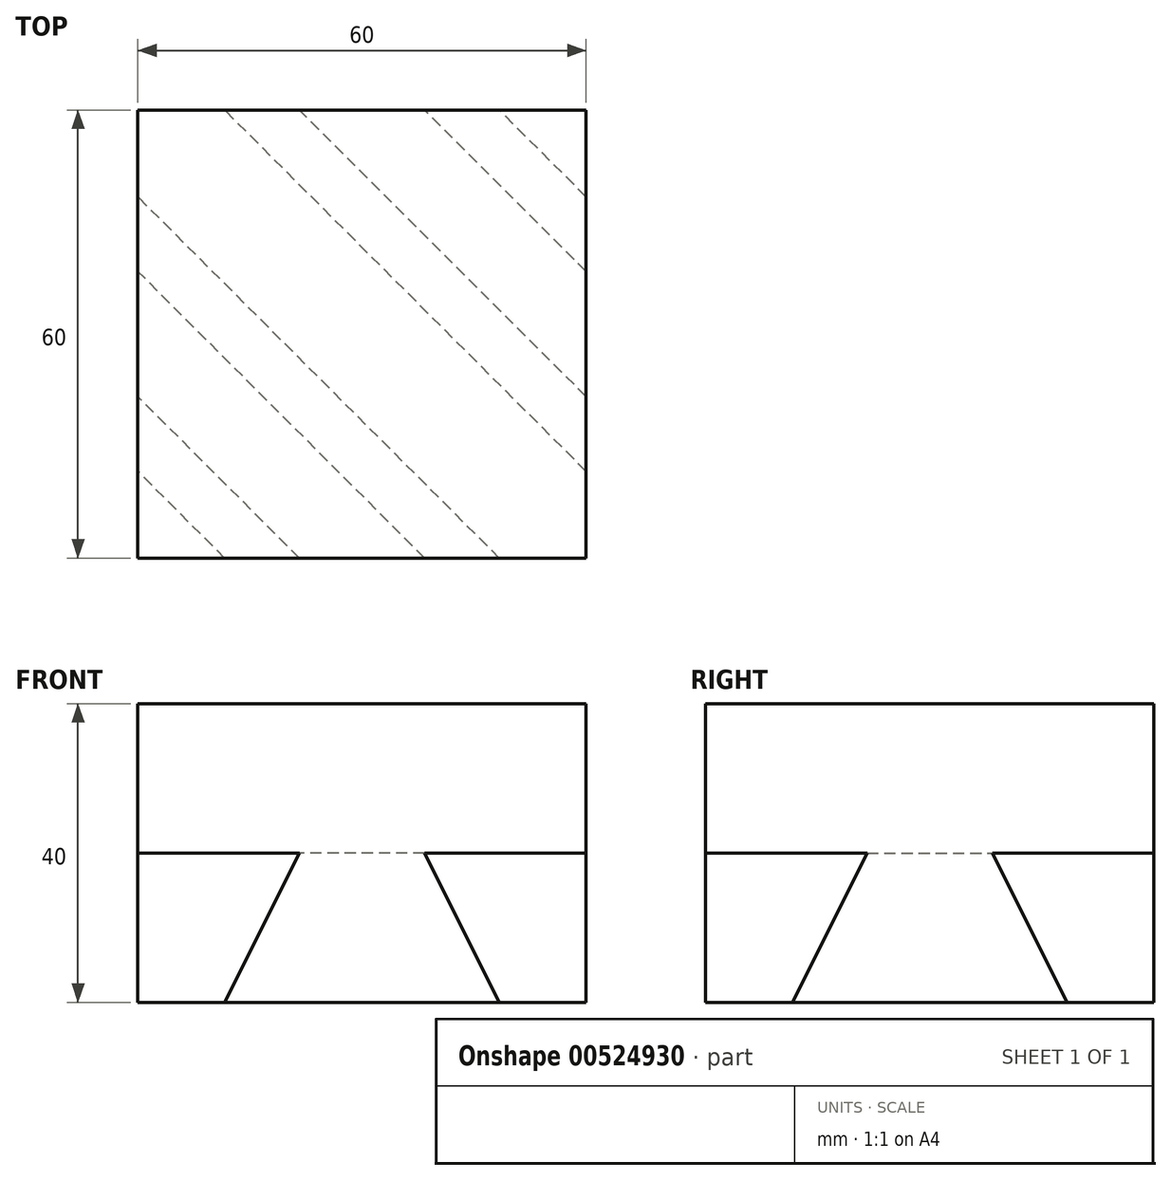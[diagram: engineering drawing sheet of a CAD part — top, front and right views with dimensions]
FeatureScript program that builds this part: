
annotation { "Feature Type Name" : "Feature", "Feature Type Description" : "" }
export const myFeature = defineFeature(function(context is Context, id is Id, definition is map)
    precondition{}
    {
        {
            var Q0;
            Q0=qCreatedBy(makeId("Front.planeOp"),FACE);
            var sketch = newSketch(context, id + "F0", { "sketchPlane" : qUnion([Q0])});
            skLineSegment(sketch, "E0", {"start": v(0, 70.49) * mm, "end": v(0, -41.75) * mm, "construction": true});
            skSolve(sketch);
        }
        {
            var Q0;
            Q0=qCreatedBy(makeId("Top.planeOp"),FACE);
            var sketch = newSketch(context, id + "F1", { "sketchPlane" : qUnion([Q0])});
            skLineSegment(sketch, "E1.bottom", {"start": v(30, 30) * mm, "end": v(-30, 30) * mm});
            skLineSegment(sketch, "E1.top", {"start": v(30, -30) * mm, "end": v(-30, -30) * mm});
            skLineSegment(sketch, "E1.left", {"start": v(30, 30) * mm, "end": v(30, -30) * mm});
            skLineSegment(sketch, "E1.right", {"start": v(-30, 30) * mm, "end": v(-30, -30) * mm});
            skPoint(sketch, "E1.middle", {"position": v(0, 0) * mm});
            skSolve(sketch);
        }
        {
            var Q0;
            Q0=qSketchRegion(id+"F1",true);
            extrude(context, id + "F2", {"entities" : qUnion([Q0]), "depth" : 60 * mm, "offsetDistance" : 25 * mm});
        }
        {
            var Q0;
            Q0=makeQuery(id+"F2.opExtrude","SWEPT_FACE",FACE,{"disambiguationData":[OSD([sQuery(id+"F1.wireOp",EDGE,"E1.top")])]});
            var sketch = newSketch(context, id + "F3", { "sketchPlane" : qUnion([Q0])});
            skLineSegment(sketch, "E2", {"start": v(-10, 40) * mm, "end": v(-20, 20) * mm, "construction": true});
            skLineSegment(sketch, "E3", {"start": v(20, 20) * mm, "end": v(10, 40) * mm, "construction": true});
            skLineSegment(sketch, "E4", {"start": v(-20, 20) * mm, "end": v(0, 20) * mm, "construction": true});
            skLineSegment(sketch, "E5", {"start": v(0, 20) * mm, "end": v(20, 20) * mm, "construction": true});
            skLineSegment(sketch, "E6", {"start": v(-10, 40) * mm, "end": v(10, 40) * mm, "construction": true});
            skLineSegment(sketch, "E7", {"start": v(-10, 40) * mm, "end": v(-30, 40) * mm, "construction": true});
            skLineSegment(sketch, "E8", {"start": v(10, 40) * mm, "end": v(30, 40) * mm, "construction": true});
            skLineSegment(sketch, "E9.0", {"start": v(-8.38, 41) * mm, "end": v(-30, 41) * mm});
            skLineSegment(sketch, "E9.1", {"start": v(-8.38, 41) * mm, "end": v(-18.38, 21) * mm});
            skLineSegment(sketch, "E9.2", {"start": v(8.38, 41) * mm, "end": v(30, 41) * mm});
            skLineSegment(sketch, "E9.3", {"start": v(18.38, 21) * mm, "end": v(8.38, 41) * mm});
            skLineSegment(sketch, "E9.4", {"start": v(0, 21) * mm, "end": v(18.38, 21) * mm});
            skLineSegment(sketch, "E9.5", {"start": v(-18.38, 21) * mm, "end": v(0, 21) * mm});
            skLineSegment(sketch, "E10", {"start": v(-8.38, 41) * mm, "end": v(8.38, 41) * mm});
            skSolve(sketch);
        }
        {
            var Q0;
            Q0=makeQuery(id+"F2.opExtrude","SWEPT_FACE",FACE,{"disambiguationData":[OSD([sQuery(id+"F1.wireOp",EDGE,"E1.left")])]});
            var sketch = newSketch(context, id + "F4", { "sketchPlane" : qUnion([Q0])});
            skLineSegment(sketch, "E11", {"start": v(-10, 40) * mm, "end": v(-20, 20) * mm, "construction": true});
            skLineSegment(sketch, "E12", {"start": v(20, 20) * mm, "end": v(10, 40) * mm, "construction": true});
            skLineSegment(sketch, "E13", {"start": v(-20, 20) * mm, "end": v(0, 20) * mm, "construction": true});
            skLineSegment(sketch, "E14", {"start": v(0, 20) * mm, "end": v(20, 20) * mm, "construction": true});
            skLineSegment(sketch, "E15", {"start": v(-10, 40) * mm, "end": v(10, 40) * mm, "construction": true});
            skLineSegment(sketch, "E16", {"start": v(-10, 40) * mm, "end": v(-30, 40) * mm, "construction": true});
            skLineSegment(sketch, "E17", {"start": v(10, 40) * mm, "end": v(30, 40) * mm, "construction": true});
            skLineSegment(sketch, "E18.0", {"start": v(-8.38, 41) * mm, "end": v(-30, 41) * mm});
            skLineSegment(sketch, "E18.1", {"start": v(-8.38, 41) * mm, "end": v(-18.38, 21) * mm});
            skLineSegment(sketch, "E18.2", {"start": v(8.38, 41) * mm, "end": v(30, 41) * mm});
            skLineSegment(sketch, "E18.3", {"start": v(18.38, 21) * mm, "end": v(8.38, 41) * mm});
            skLineSegment(sketch, "E18.4", {"start": v(0, 21) * mm, "end": v(18.38, 21) * mm});
            skLineSegment(sketch, "E18.5", {"start": v(-18.38, 21) * mm, "end": v(0, 21) * mm});
            skLineSegment(sketch, "E19", {"start": v(-8.38, 41) * mm, "end": v(8.38, 41) * mm});
            skSolve(sketch);
        }
        {
            var Q0;
            Q0=makeQuery(id+"F2.opExtrude","SWEPT_FACE",FACE,{"disambiguationData":[OSD([sQuery(id+"F1.wireOp",EDGE,"E1.bottom")])]});
            var sketch = newSketch(context, id + "F5", { "sketchPlane" : qUnion([Q0])});
            skLineSegment(sketch, "E20", {"start": v(-10, 40) * mm, "end": v(-20, 20) * mm, "construction": true});
            skLineSegment(sketch, "E21", {"start": v(20, 20) * mm, "end": v(10, 40) * mm, "construction": true});
            skLineSegment(sketch, "E22", {"start": v(-20, 20) * mm, "end": v(0, 20) * mm, "construction": true});
            skLineSegment(sketch, "E23", {"start": v(0, 20) * mm, "end": v(20, 20) * mm, "construction": true});
            skLineSegment(sketch, "E24", {"start": v(-10, 40) * mm, "end": v(10, 40) * mm, "construction": true});
            skLineSegment(sketch, "E25", {"start": v(-10, 40) * mm, "end": v(-30, 40) * mm, "construction": true});
            skLineSegment(sketch, "E26", {"start": v(10, 40) * mm, "end": v(30, 40) * mm, "construction": true});
            skLineSegment(sketch, "E27.0", {"start": v(-8.38, 41) * mm, "end": v(-30, 41) * mm});
            skLineSegment(sketch, "E27.1", {"start": v(-8.38, 41) * mm, "end": v(-18.38, 21) * mm});
            skLineSegment(sketch, "E27.2", {"start": v(8.38, 41) * mm, "end": v(30, 41) * mm});
            skLineSegment(sketch, "E27.3", {"start": v(18.38, 21) * mm, "end": v(8.38, 41) * mm});
            skLineSegment(sketch, "E27.4", {"start": v(0, 21) * mm, "end": v(18.38, 21) * mm});
            skLineSegment(sketch, "E27.5", {"start": v(-18.38, 21) * mm, "end": v(0, 21) * mm});
            skLineSegment(sketch, "E28", {"start": v(8.38, 41) * mm, "end": v(-8.38, 41) * mm});
            skSolve(sketch);
        }
        {
            var Q0;
            Q0=makeQuery(id+"F2.opExtrude","SWEPT_FACE",FACE,{"disambiguationData":[OSD([sQuery(id+"F1.wireOp",EDGE,"E1.right")])]});
            var sketch = newSketch(context, id + "F6", { "sketchPlane" : qUnion([Q0])});
            skLineSegment(sketch, "E29", {"start": v(-10, 40) * mm, "end": v(-20, 20) * mm, "construction": true});
            skLineSegment(sketch, "E30", {"start": v(20, 20) * mm, "end": v(10, 40) * mm, "construction": true});
            skLineSegment(sketch, "E31", {"start": v(-20, 20) * mm, "end": v(0, 20) * mm, "construction": true});
            skLineSegment(sketch, "E32", {"start": v(0, 20) * mm, "end": v(20, 20) * mm, "construction": true});
            skLineSegment(sketch, "E33", {"start": v(-10, 40) * mm, "end": v(10, 40) * mm, "construction": true});
            skLineSegment(sketch, "E34", {"start": v(-10, 40) * mm, "end": v(-30, 40) * mm, "construction": true});
            skLineSegment(sketch, "E35", {"start": v(10, 40) * mm, "end": v(30, 40) * mm, "construction": true});
            skLineSegment(sketch, "E36.0", {"start": v(-8.38, 41) * mm, "end": v(-30, 41) * mm});
            skLineSegment(sketch, "E36.1", {"start": v(-8.38, 41) * mm, "end": v(-18.38, 21) * mm});
            skLineSegment(sketch, "E36.2", {"start": v(8.38, 41) * mm, "end": v(30, 41) * mm});
            skLineSegment(sketch, "E36.3", {"start": v(18.38, 21) * mm, "end": v(8.38, 41) * mm});
            skLineSegment(sketch, "E36.4", {"start": v(0, 21) * mm, "end": v(18.38, 21) * mm});
            skLineSegment(sketch, "E36.5", {"start": v(-18.38, 21) * mm, "end": v(0, 21) * mm});
            skLineSegment(sketch, "E37", {"start": v(-8.38, 41) * mm, "end": v(8.38, 41) * mm});
            skSolve(sketch);
        }
        {
            var Q1;
            Q1=makeQuery(id+"F3.imprint","IMPRINT",FACE,{"disambiguationData":[TD([[makeQuery(id+"F3.imprint","IMPRINT",EDGE,{"derivedFrom":sQuery(id+"F3.wireOp",EDGE,"E9.1")}),1.0]])]});
            var Q2;
            Q2=makeQuery(id+"F6.imprint","IMPRINT",FACE,{"disambiguationData":[TD([[makeQuery(id+"F6.imprint","IMPRINT",EDGE,{"derivedFrom":sQuery(id+"F6.wireOp",EDGE,"E36.1")}),1.0]])]});
            loft(context, id + "F7", {"operationType" : NewBodyOperationType.REMOVE, "sheetProfilesArray" : [{ "sheetProfileEntities" : qUnion([Q1]) }, { "sheetProfileEntities" : qUnion([Q2]) }]});
        }
        {
            var Q1;
            Q1=makeQuery(id+"F4.imprint","IMPRINT",FACE,{"disambiguationData":[TD([[makeQuery(id+"F4.imprint","IMPRINT",EDGE,{"derivedFrom":sQuery(id+"F4.wireOp",EDGE,"E18.1")}),1.0]])]});
            var Q2;
            Q2=makeQuery(id+"F5.imprint","IMPRINT",FACE,{"disambiguationData":[TD([[makeQuery(id+"F5.imprint","IMPRINT",EDGE,{"derivedFrom":sQuery(id+"F5.wireOp",EDGE,"E27.1")}),1.0]])]});
            loft(context, id + "F8", {"operationType" : NewBodyOperationType.REMOVE, "sheetProfilesArray" : [{ "sheetProfileEntities" : qUnion([Q1]) }, { "sheetProfileEntities" : qUnion([Q2]) }]});
        }
        {
            var Q0;
            Q0=makeQuery(id+"F2.opExtrude","SWEPT_FACE",FACE,{"disambiguationData":[OSD([sQuery(id+"F1.wireOp",EDGE,"E1.top")])]});
            var sketch = newSketch(context, id + "F9", { "sketchPlane" : qUnion([Q0])});
            skLineSegment(sketch, "E38.bottom", {"start": v(-30, 60) * mm, "end": v(30, 60) * mm});
            skLineSegment(sketch, "E38.top", {"start": v(-30, 41) * mm, "end": v(30, 41) * mm});
            skLineSegment(sketch, "E38.left", {"start": v(-30, 60) * mm, "end": v(-30, 41) * mm});
            skLineSegment(sketch, "E38.right", {"start": v(30, 60) * mm, "end": v(30, 41) * mm});
            skSolve(sketch);
        }
        {
            var Q0;
            Q0 = qSketchRegion(id + "F9", true);
            extrude(context, id + "F10", {"entities" : qUnion([Q0]), "operationType" : NewBodyOperationType.REMOVE, "oppositeDirection" : true, "depth" : 60 * mm, "offsetDistance" : 25 * mm});
        }
        {
            var Q0;
            Q0=makeQuery(id+"F10.boolean.opBoolean","COPY",FACE,{"disambiguationData":[TD([makeQuery(id+"F7.boolean.opBoolean","COPY",FACE,{"derivedFrom":makeQuery(id+"F7.opLoft","SWEPT_FACE",FACE,{"disambiguationData":[OSD([sQuery(id+"F3.wireOp",EDGE,"E9.2"),sQuery(id+"F3.wireOp",EDGE,"E9.3"),sQuery(id+"F3.wireOp",EDGE,"E9.4"),sQuery(id+"F3.wireOp",EDGE,"E10"),sQuery(id+"F6.wireOp",EDGE,"E36.0"),sQuery(id+"F6.wireOp",EDGE,"E36.1"),sQuery(id+"F6.wireOp",EDGE,"E36.5"),sQuery(id+"F6.wireOp",EDGE,"E37")])]})})])],"derivedFrom":makeQuery(id+"F10.opExtrude","SWEPT_FACE",FACE,{"disambiguationData":[OSD([sQuery(id+"F9.wireOp",EDGE,"E38.top")])]})});
            var sketch = newSketch(context, id + "F11", { "sketchPlane" : qUnion([Q0])});
            skLineSegment(sketch, "E39.bottom", {"start": v(-30, 30) * mm, "end": v(30, 30) * mm});
            skLineSegment(sketch, "E39.top", {"start": v(-30, -30) * mm, "end": v(30, -30) * mm});
            skLineSegment(sketch, "E39.left", {"start": v(-30, 30) * mm, "end": v(-30, -30) * mm});
            skLineSegment(sketch, "E39.right", {"start": v(30, 30) * mm, "end": v(30, -30) * mm});
            skSolve(sketch);
        }
        {
            var Q0;
            Q0 = qSketchRegion(id + "F11", true);
            extrude(context, id + "F12", {"entities" : qUnion([Q0]), "endBound" : BoundingType.SYMMETRIC, "depth" : 40 * mm, "offsetDistance" : 25 * mm});
        }
        {
            var Q0;
            Q0=makeQuery(id+"F2.opExtrude","SWEPT_BODY",BODY,{"disambiguationData":[OSD([sQuery(id+"F1.wireOp",EDGE,"E1.bottom"),sQuery(id+"F1.wireOp",EDGE,"E1.top"),sQuery(id+"F1.wireOp",EDGE,"E1.left"),sQuery(id+"F1.wireOp",EDGE,"E1.right")])]});
            var Q1;
            Q1=makeQuery(id+"F12.opExtrude","SWEPT_BODY",BODY,{"disambiguationData":[OSD([sQuery(id+"F11.wireOp",EDGE,"E39.bottom"),sQuery(id+"F11.wireOp",EDGE,"E39.top"),sQuery(id+"F11.wireOp",EDGE,"E39.left"),sQuery(id+"F11.wireOp",EDGE,"E39.right")])]});
            booleanBodies(context, id + "F13", {"operationType" : BooleanOperationType.SUBTRACTION, "tools" : qUnion([Q0]), "targets" : qUnion([Q1])});
        }
    });
